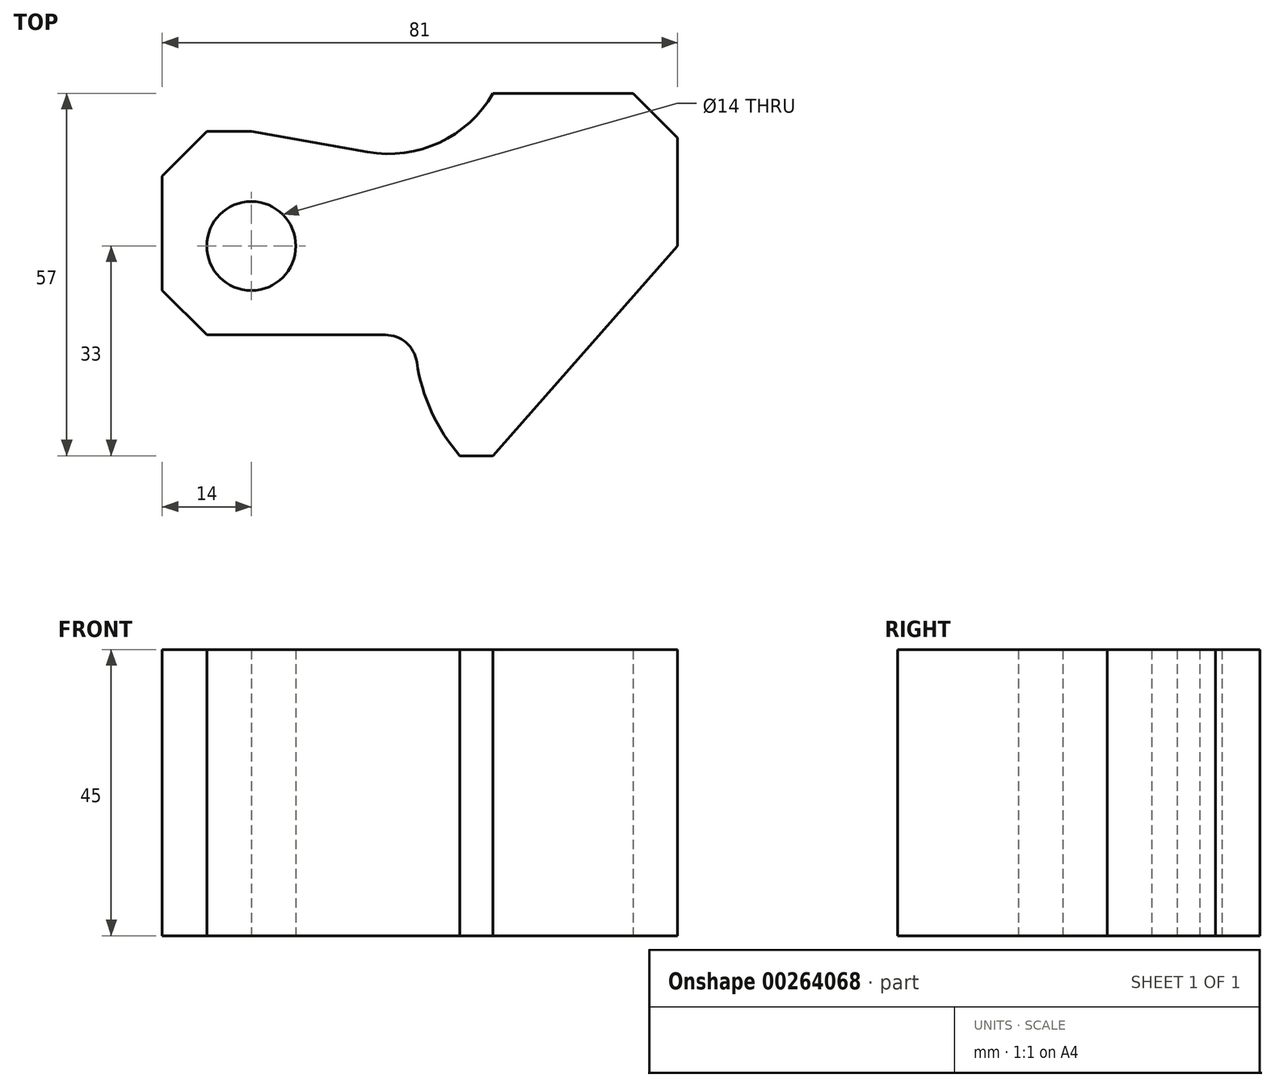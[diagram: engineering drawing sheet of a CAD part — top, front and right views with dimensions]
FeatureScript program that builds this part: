
annotation { "Feature Type Name" : "Feature", "Feature Type Description" : "" }
export const myFeature = defineFeature(function(context is Context, id is Id, definition is map)
    precondition{}
    {
        {
            var Q0;
            Q0=qCreatedBy(makeId("Top.planeOp"),FACE);
            var sketch = newSketch(context, id + "F0", { "sketchPlane" : qUnion([Q0])});
            skCircle(sketch, "E0", {"center": v(0, 0) * mm, "radius": 7 * mm});
            skLineSegment(sketch, "E1", {"start": v(-14, 11) * mm, "end": v(-14, -7) * mm});
            skLineSegment(sketch, "E2", {"start": v(-14, -7) * mm, "end": v(-7, -14) * mm});
            skLineSegment(sketch, "E3", {"start": v(-14, 11) * mm, "end": v(-7, 18) * mm});
            skLineSegment(sketch, "E4", {"start": v(-7, 18) * mm, "end": v(0, 18) * mm});
            skLineSegment(sketch, "E5", {"start": v(0, 18) * mm, "end": v(18.24, 14.78) * mm});
            skLineSegment(sketch, "E6", {"start": v(67, 0) * mm, "end": v(67, 17) * mm});
            skLineSegment(sketch, "E7", {"start": v(67, 17) * mm, "end": v(60, 24) * mm});
            skLineSegment(sketch, "E8", {"start": v(60, 24) * mm, "end": v(38, 24) * mm});
            skArc(sketch, "E9", {"start": v(18.24, 14.78) * mm, "mid": v(29.57, 16.28) * mm, "end": v(38, 24) * mm});
            skLineSegment(sketch, "E10", {"start": v(-14, -27.27) * mm, "end": v(-14, 32.25) * mm, "construction": true});
            skLineSegment(sketch, "E11", {"start": v(67, 17) * mm, "end": v(67, 47) * mm, "construction": true});
            skLineSegment(sketch, "E12", {"start": v(0, 18) * mm, "end": v(21.95, 18) * mm, "construction": true});
            skLineSegment(sketch, "E13", {"start": v(38, -33) * mm, "end": v(67, 0) * mm});
            skLineSegment(sketch, "E14", {"start": v(38, -33) * mm, "end": v(32.79, -33) * mm});
            skLineSegment(sketch, "E15", {"start": v(-7, -14) * mm, "end": v(21.07, -14) * mm});
            skArc(sketch, "E16", {"start": v(26.01, -18.26) * mm, "mid": v(24.33, -15.21) * mm, "end": v(21.07, -14) * mm});
            skArc(sketch, "E17", {"start": v(26.01, -18.26) * mm, "mid": v(28.35, -26.12) * mm, "end": v(32.79, -33) * mm});
            skSolve(sketch);
        }
        {
            var Q0;
            Q0 = qSketchRegion(id + "F0", true);
            extrude(context, id + "F1", {"entities" : qUnion([Q0]), "depth" : 45 * mm});
        }
    });
